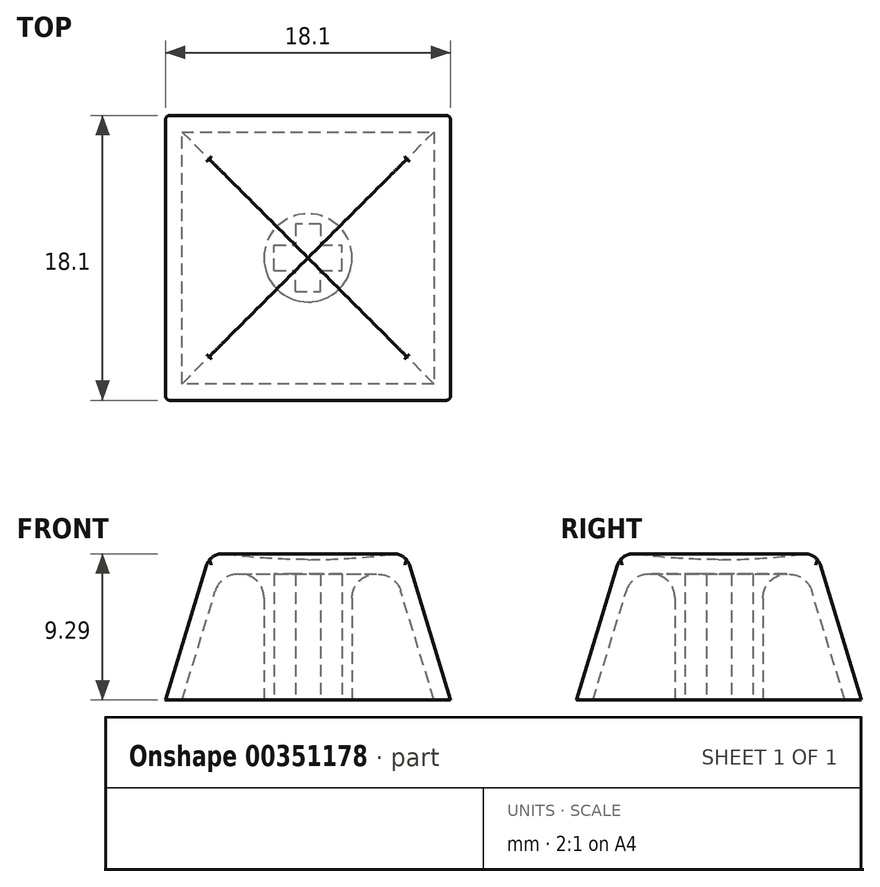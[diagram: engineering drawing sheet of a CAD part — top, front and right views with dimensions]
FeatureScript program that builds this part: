
annotation { "Feature Type Name" : "Feature", "Feature Type Description" : "" }
export const myFeature = defineFeature(function(context is Context, id is Id, definition is map)
    precondition{}
    {
        {
            var Q0;
            Q0=qCreatedBy(makeId("Front.planeOp"),FACE);
            var sketch = newSketch(context, id + "F0", { "sketchPlane" : qUnion([Q0])});
            skLineSegment(sketch, "E0", {"start": v(-8, 0) * mm, "end": v(-5.57, 8) * mm});
            skLineSegment(sketch, "E1", {"start": v(-5.57, 8) * mm, "end": v(5.57, 8) * mm});
            skLineSegment(sketch, "E2", {"start": v(5.57, 8) * mm, "end": v(8, 0) * mm});
            skLineSegment(sketch, "E3", {"start": v(8, 0) * mm, "end": v(9.05, 0) * mm});
            skLineSegment(sketch, "E4", {"start": v(9.05, 0) * mm, "end": v(6.18, 9.4) * mm});
            skLineSegment(sketch, "E5", {"start": v(-6.19, 9.4) * mm, "end": v(-9.05, 0) * mm});
            skLineSegment(sketch, "E6", {"start": v(-9.05, 0) * mm, "end": v(-8, 0) * mm});
            skArc(sketch, "E7", {"start": v(-6.19, 9.4) * mm, "mid": v(0, 8.92) * mm, "end": v(6.19, 9.4) * mm});
            skSolve(sketch);
        }
        {
            var Q0;
            Q0=qCreatedBy(makeId("Top.planeOp"),FACE);
            var sketch = newSketch(context, id + "F1", { "sketchPlane" : qUnion([Q0])});
            skLineSegment(sketch, "E8.0", {"start": v(-9.05, 0) * mm, "end": v(-8, 0) * mm});
            skLineSegment(sketch, "E9.0", {"start": v(8, 0) * mm, "end": v(9.05, 0) * mm});
            skLineSegment(sketch, "E10.bottom", {"start": v(-8.53, 8.53) * mm, "end": v(8.53, 8.53) * mm});
            skLineSegment(sketch, "E10.top", {"start": v(-8.53, -8.53) * mm, "end": v(8.53, -8.53) * mm});
            skLineSegment(sketch, "E10.left", {"start": v(-8.53, 8.53) * mm, "end": v(-8.53, -8.53) * mm});
            skLineSegment(sketch, "E10.right", {"start": v(8.53, 8.53) * mm, "end": v(8.53, -8.53) * mm});
            skPoint(sketch, "E10.middle", {"position": v(0, 0) * mm});
            skSolve(sketch);
        }
        {
            var Q0;
            Q0=makeQuery(id+"F0.imprint","IMPRINT",FACE,{"disambiguationData":[TD([[makeQuery(id+"F0.imprint","IMPRINT",EDGE,{"derivedFrom":sQuery(id+"F0.wireOp",EDGE,"E0")}),1.0]])]});
            var Q1;
            Q1=sQuery(id+"F1.wireOp",EDGE,"E10.left");
            var Q2;
            Q2=sQuery(id+"F1.wireOp",EDGE,"E10.bottom");
            var Q3;
            Q3=sQuery(id+"F1.wireOp",EDGE,"E10.right");
            var Q4;
            Q4=sQuery(id+"F1.wireOp",EDGE,"E10.top");
            sweep(context, id + "F2", {"profiles" : qUnion([Q0]), "path" : qUnion([Q1, Q2, Q3, Q4])});
        }
        {
            var Q0;
            Q0=qCreatedBy(makeId("Top.planeOp"),FACE);
            var sketch = newSketch(context, id + "F3", { "sketchPlane" : qUnion([Q0])});
            skCircle(sketch, "E11", {"center": v(0, 0) * mm, "radius": 2.8 * mm});
            skLineSegment(sketch, "E12.bottom", {"start": v(-2.15, -0.8) * mm, "end": v(-0.8, -0.8) * mm});
            skLineSegment(sketch, "E12.top", {"start": v(-2.15, 0.8) * mm, "end": v(-0.8, 0.8) * mm});
            skLineSegment(sketch, "E12.left", {"start": v(-2.15, -0.8) * mm, "end": v(-2.15, 0.8) * mm});
            skLineSegment(sketch, "E12.right", {"start": v(2.15, -0.8) * mm, "end": v(2.15, 0.8) * mm});
            skLineSegment(sketch, "E13.bottom", {"start": v(-0.8, -2.15) * mm, "end": v(0.8, -2.15) * mm});
            skLineSegment(sketch, "E13.top", {"start": v(-0.8, 2.15) * mm, "end": v(0.8, 2.15) * mm});
            skLineSegment(sketch, "E13.right", {"start": v(0.8, -2.15) * mm, "end": v(0.8, -0.8) * mm});
            skLineSegment(sketch, "E14.trimOffspring", {"start": v(0.8, 0.8) * mm, "end": v(0.8, 2.15) * mm});
            skLineSegment(sketch, "E15.trimOffspring", {"start": v(0.8, -0.8) * mm, "end": v(2.15, -0.8) * mm});
            skLineSegment(sketch, "E16.trimOffspring", {"start": v(-0.8, 0.8) * mm, "end": v(-0.8, 2.15) * mm});
            skLineSegment(sketch, "E17.trimOffspring", {"start": v(0.8, 0.8) * mm, "end": v(2.15, 0.8) * mm});
            skLineSegment(sketch, "E18", {"start": v(-0.8, -2.15) * mm, "end": v(-0.8, -0.8) * mm});
            skSolve(sketch);
        }
        {
            var Q0;
            Q0=makeQuery(id+"F3.imprint","IMPRINT",FACE,{"disambiguationData":[TD([[makeQuery(id+"F3.imprint","IMPRINT",EDGE,{"derivedFrom":sQuery(id+"F3.wireOp",EDGE,"E11")}),1.0]])]});
            var Q1;
            Q1=makeQuery(id+"F2.opSweep","SWEPT_FACE",FACE,{"disambiguationData":[OSD([sQuery(id+"F0.wireOp",EDGE,"E1"),sQuery(id+"F1.wireOp",EDGE,"E10.left")])]});
            extrude(context, id + "F4", {"entities" : qUnion([Q0]), "operationType" : NewBodyOperationType.ADD, "endBound" : BoundingType.UP_TO_SURFACE, "endBoundEntityFace" : qUnion([Q1]), "depth" : 25 * mm});
        }
        {
            var Q0;
            Q0=makeQuery(id+"F2.opSweep","SWEPT_EDGE",EDGE,{"disambiguationData":[OSD([sQuery(id+"F0.wireOp",EDGE,"E4"),sQuery(id+"F0.wireOp",EDGE,"E7"),sQuery(id+"F1.wireOp",EDGE,"E10.right")])]});
            var Q1;
            Q1=makeQuery(id+"F2.opSweep","SWEPT_EDGE",EDGE,{"disambiguationData":[OSD([sQuery(id+"F0.wireOp",EDGE,"E4"),sQuery(id+"F0.wireOp",EDGE,"E7"),sQuery(id+"F1.wireOp",EDGE,"E10.bottom")])]});
            var Q2;
            Q2=makeQuery(id+"F2.opSweep","SWEPT_EDGE",EDGE,{"disambiguationData":[OSD([sQuery(id+"F0.wireOp",EDGE,"E4"),sQuery(id+"F0.wireOp",EDGE,"E7"),sQuery(id+"F1.wireOp",EDGE,"E10.left")])]});
            var Q3;
            Q3=makeQuery(id+"F2.opSweep","SWEPT_EDGE",EDGE,{"disambiguationData":[OSD([sQuery(id+"F0.wireOp",EDGE,"E4"),sQuery(id+"F0.wireOp",EDGE,"E7"),sQuery(id+"F1.wireOp",EDGE,"E10.top")])]});
            fillet(context, id + "F5", {"entities" : qUnion([Q0, Q1, Q2, Q3]), "radius" : 1 * mm, "tangentPropagation" : true, "allowEdgeOverflow" : false});
        }
        {
            var Q0;
            Q0=makeQuery(id+"F2.opSweep","MID_CAP_EDGE",EDGE,{"disambiguationData":[OSD([sQuery(id+"F0.wireOp",EDGE,"E4"),sQuery(id+"F1.wireOp",VERTEX,"E10.top.start")])],"capPos":2.0});
            var Q1;
            Q1=makeQuery(id+"F2.opSweep","MID_CAP_EDGE",EDGE,{"disambiguationData":[OSD([sQuery(id+"F0.wireOp",EDGE,"E4"),sQuery(id+"F1.wireOp",VERTEX,"E10.top.end")])],"capPos":1.0});
            var Q2;
            Q2=makeQuery(id+"F2.opSweep","CAP_EDGE",EDGE,{"disambiguationData":[OSD([sQuery(id+"F0.wireOp",EDGE,"E4"),sQuery(id+"F1.wireOp",VERTEX,"E10.right.start")])],"isStart":true});
            var Q3;
            Q3=makeQuery(id+"F2.opSweep","MID_CAP_EDGE",EDGE,{"disambiguationData":[OSD([sQuery(id+"F0.wireOp",EDGE,"E4"),sQuery(id+"F1.wireOp",VERTEX,"E10.bottom.start")])],"capPos":3.0});
            fillet(context, id + "F6", {"entities" : qUnion([Q0, Q1, Q2, Q3]), "radius" : 0.3 * mm, "tangentPropagation" : true, "allowEdgeOverflow" : false});
        }
        {
            var Q0;
            Q0=makeQuery(id+"F4.opExtrude","CAP_EDGE",EDGE,{"disambiguationData":[OSD([sQuery(id+"F3.wireOp",EDGE,"E11")])],"isStart":false});
            var Q1;
            Q1=makeQuery(id+"F2.opSweep","SWEPT_EDGE",EDGE,{"disambiguationData":[OSD([sQuery(id+"F0.wireOp",EDGE,"E1"),sQuery(id+"F0.wireOp",EDGE,"E2"),sQuery(id+"F1.wireOp",EDGE,"E10.right")])]});
            var Q2;
            Q2=makeQuery(id+"F2.opSweep","SWEPT_EDGE",EDGE,{"disambiguationData":[OSD([sQuery(id+"F0.wireOp",EDGE,"E1"),sQuery(id+"F0.wireOp",EDGE,"E2"),sQuery(id+"F1.wireOp",EDGE,"E10.top")])]});
            var Q3;
            Q3=makeQuery(id+"F2.opSweep","SWEPT_EDGE",EDGE,{"disambiguationData":[OSD([sQuery(id+"F0.wireOp",EDGE,"E1"),sQuery(id+"F0.wireOp",EDGE,"E2"),sQuery(id+"F1.wireOp",EDGE,"E10.left")])]});
            var Q4;
            Q4=makeQuery(id+"F2.opSweep","SWEPT_EDGE",EDGE,{"disambiguationData":[OSD([sQuery(id+"F0.wireOp",EDGE,"E1"),sQuery(id+"F0.wireOp",EDGE,"E2"),sQuery(id+"F1.wireOp",EDGE,"E10.bottom")])]});
            fillet(context, id + "F7", {"entities" : qUnion([Q0, Q1, Q2, Q3, Q4]), "radius" : 1.5 * mm, "tangentPropagation" : true, "allowEdgeOverflow" : false});
        }
    });
